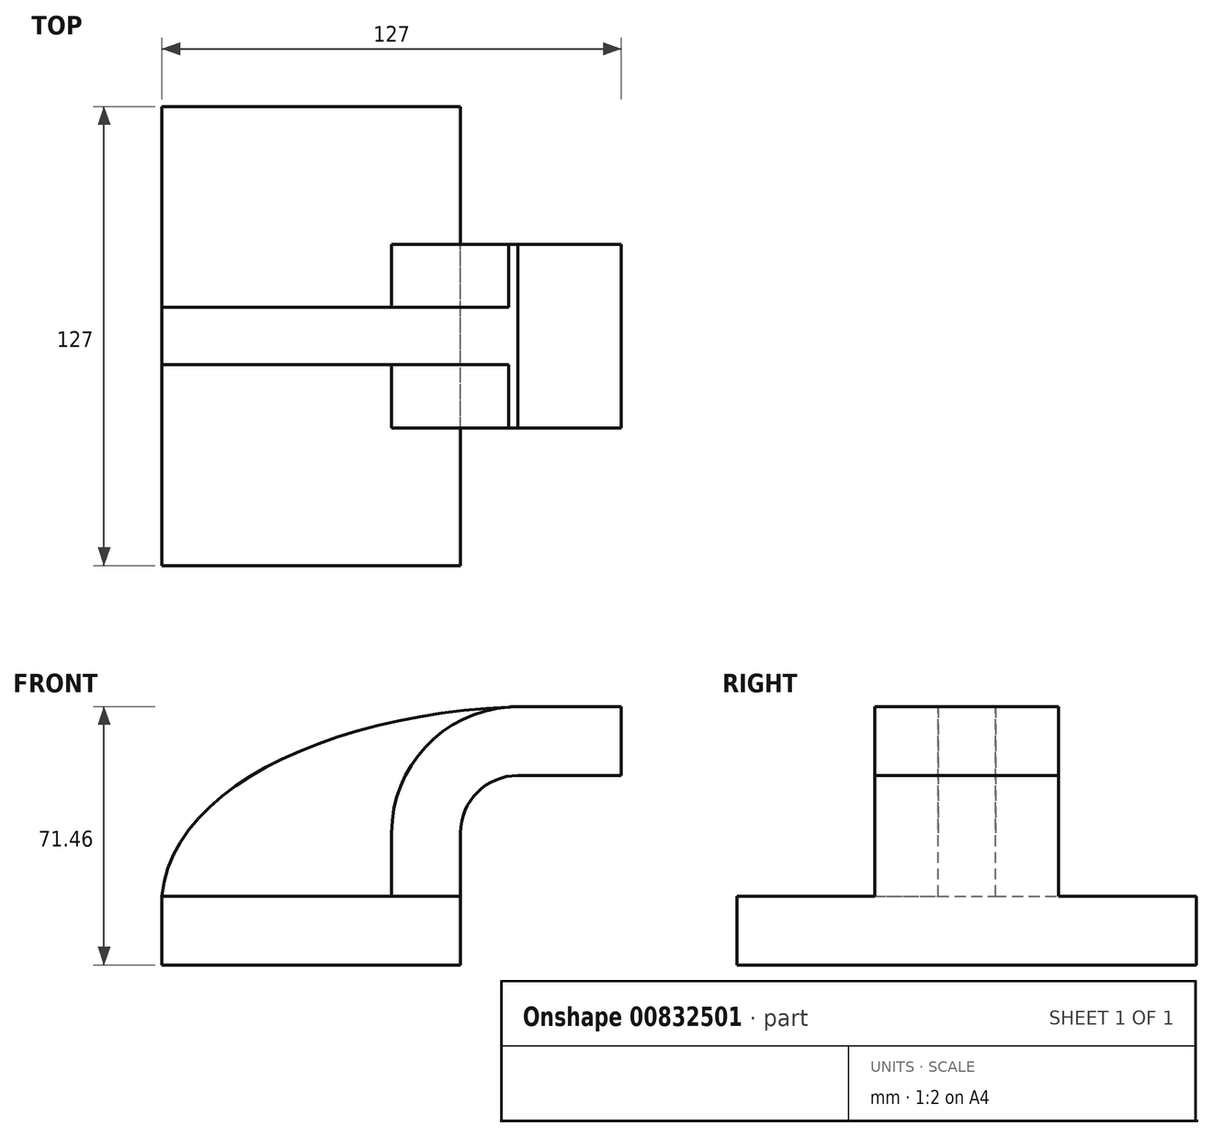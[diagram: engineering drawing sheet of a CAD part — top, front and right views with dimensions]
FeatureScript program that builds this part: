
annotation { "Feature Type Name" : "Feature", "Feature Type Description" : "" }
export const myFeature = defineFeature(function(context is Context, id is Id, definition is map)
    precondition{}
    {
        {
            var Q0;
            Q0=qCreatedBy(makeId("Front.planeOp"),FACE);
            var sketch = newSketch(context, id + "F0", { "sketchPlane" : qUnion([Q0])});
            skLineSegment(sketch, "E0.bottom", {"start": v(-41.27, -9.53) * mm, "end": v(41.28, -9.53) * mm});
            skLineSegment(sketch, "E0.top", {"start": v(-41.28, 9.52) * mm, "end": v(41.28, 9.52) * mm});
            skLineSegment(sketch, "E0.left", {"start": v(-41.28, -9.53) * mm, "end": v(-41.28, 9.53) * mm});
            skLineSegment(sketch, "E0.right", {"start": v(41.28, -9.53) * mm, "end": v(41.28, 9.52) * mm});
            skPoint(sketch, "E0.middle", {"position": v(0, 0) * mm});
            skLineSegment(sketch, "E1.bottom", {"start": v(60.33, 38.1) * mm, "end": v(111.13, 38.1) * mm});
            skLineSegment(sketch, "E1.top", {"start": v(60.33, 66.68) * mm, "end": v(111.13, 66.68) * mm});
            skLineSegment(sketch, "E1.left", {"start": v(60.33, 38.1) * mm, "end": v(60.33, 66.68) * mm});
            skLineSegment(sketch, "E1.right", {"start": v(111.13, 38.1) * mm, "end": v(111.13, 66.68) * mm});
            skPoint(sketch, "E1.middle", {"position": v(85.73, 52.39) * mm});
            skLineSegment(sketch, "E2", {"start": v(41.28, 9.52) * mm, "end": v(41.28, 27) * mm});
            skArc(sketch, "E3", {"start": v(41.27, 27) * mm, "mid": v(45.92, 38.23) * mm, "end": v(57.15, 42.88) * mm});
            skLineSegment(sketch, "E4", {"start": v(57.15, 42.88) * mm, "end": v(85.72, 42.88) * mm});
            skLineSegment(sketch, "E5.0", {"start": v(57.15, 61.93) * mm, "end": v(85.72, 61.93) * mm});
            skArc(sketch, "E5.1", {"start": v(22.22, 27) * mm, "mid": v(32.45, 51.7) * mm, "end": v(57.15, 61.93) * mm});
            skLineSegment(sketch, "E5.2", {"start": v(22.22, 9.52) * mm, "end": v(22.22, 27) * mm});
            skLineSegment(sketch, "E6", {"start": v(85.72, 42.88) * mm, "end": v(85.72, 61.93) * mm});
            skFitSpline(sketch, "E7", {"points": [v(-41.28, 9.53) * mm, v(57.15, 61.93) * mm], "startDerivative": vector(8.29, 92.68) * mm, "endDerivative": vector(146.8, 4.36) * mm});
            skSolve(sketch);
        }
        {
            var Q0;
            Q0=makeQuery(id+"F0.imprint","IMPRINT",FACE,{"disambiguationData":[TD([[makeQuery(id+"F0.imprint","IMPRINT",EDGE,{"derivedFrom":sQuery(id+"F0.wireOp",EDGE,"E0.bottom")}),1.0]])]});
            extrude(context, id + "F1", {"entities" : qUnion([Q0]), "endBound" : BoundingType.SYMMETRIC, "depth" : 127 * mm, "offsetDistance" : 25.4 * mm});
        }
        {
            var Q0;
            {var subQ0=sQuery(id+"F0.wireOp",EDGE,"E2");Q0=makeQuery(id+"F0.imprint","IMPRINT",FACE,{"disambiguationData":[TD([[makeQuery(id+"F0.imprint","IMPRINT",EDGE,{"derivedFrom":subQ0}),1.0]])]});}
            extrude(context, id + "F2", {"entities" : qUnion([Q0]), "operationType" : NewBodyOperationType.ADD, "endBound" : BoundingType.SYMMETRIC, "depth" : 50.8 * mm, "offsetDistance" : 25.4 * mm});
        }
        {
            var Q0;
            {var subQ5=sQuery(id+"F0.wireOp",EDGE,"E6");Q0=makeQuery(id+"F0.imprint","IMPRINT",FACE,{"disambiguationData":[TD([[makeQuery(id+"F0.imprint","IMPRINT",EDGE,{"derivedFrom":subQ5}),1.0]])]});}
            extrude(context, id + "F3", {"entities" : qUnion([Q0]), "operationType" : NewBodyOperationType.ADD, "endBound" : BoundingType.SYMMETRIC, "depth" : 50.8 * mm, "offsetDistance" : 25.4 * mm});
        }
        {
            var Q0;
            {var subQ3=sQuery(id+"F0.wireOp",EDGE,"E5.2");Q0=makeQuery(id+"F0.imprint","IMPRINT",FACE,{"disambiguationData":[TD([[makeQuery(id+"F0.imprint","IMPRINT",EDGE,{"derivedFrom":subQ3}),1.0]])]});}
            extrude(context, id + "F4", {"entities" : qUnion([Q0]), "operationType" : NewBodyOperationType.ADD, "endBound" : BoundingType.SYMMETRIC, "depth" : 15.88 * mm, "offsetDistance" : 25.4 * mm});
        }
    });
